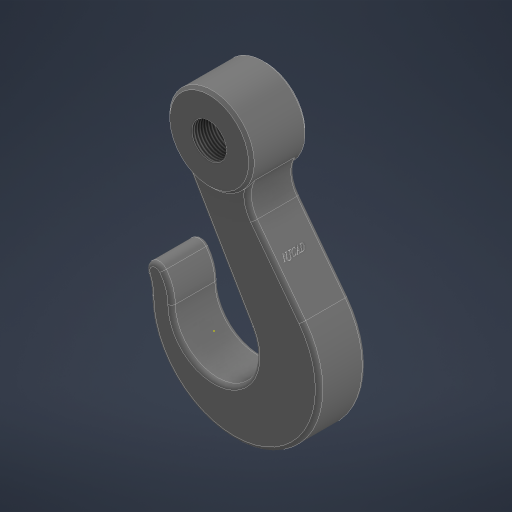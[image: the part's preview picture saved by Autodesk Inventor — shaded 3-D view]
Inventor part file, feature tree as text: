
AUTODESK INVENTOR PART (.ipt)
format: ipt  version: 2023 (Build 270158000, 158)  size: 479,744 bytes
history: native  units: mm
features: sketch x6, emboss x3, extrude x1, hole x1, fillet x1, chamfer x1
ambient origin geometry x8: Origin, YZ Plane, XZ Plane, XY Plane, X Axis, Y Axis, Z Axis, Center Point
bodies: Solid1 (feature_tree)
feature tree (13):
  extrude  "Extrusion1"  Depth=180.0mm
  emboss  "Emboss1"
  emboss  "Emboss2"
  hole  "Hole2"  [1 undecoded]
  fillet  "Fillet1"  Radius=178.0mm
  chamfer  "Chamfer1"  Distance=50.0mm
  sketch  "Sketch8"  dims[d16=45.0mm]
  emboss  "Emboss3"
  sketch  "Sketch2"  dims[d9=90.0mm d10=180.0mm]
  sketch  "Sketch5"  dims[d11=22.0mm d12=90.0mm d13=178.0mm]
  sketch  "Sketch6"  dims[d14=32.0mm]
  sketch  "Sketch7"  dims[d15=45.0mm]
  sketch  "Sketch9"  dims[d17=10.0mm d18=50.0mm d19=0.0mm d29=90.0mm d30=5.0mm d31=0.0mm d32=90.0mm d33=5.0mm d34=0.0mm d35=36.752404mm d36=80.0mm d37=20.0mm d38=2.0mm d39=90.0deg d40=8.0mm d41=20.594885mm d42=4.0mm d43=3.0mm d44=3.0mm d45=45.0deg d46=1.0mm d47=0.0mm d48=14.3117mm d49=0.75mm d50=20.594885mm d51=0.0625mm d52=0.75mm d53=0.375mm]
note: 1 required parameter value undecoded (feature->parameter linkage not recoverable at this tier; creation-order binding heuristic only, values carry confidence <= 0.55)
